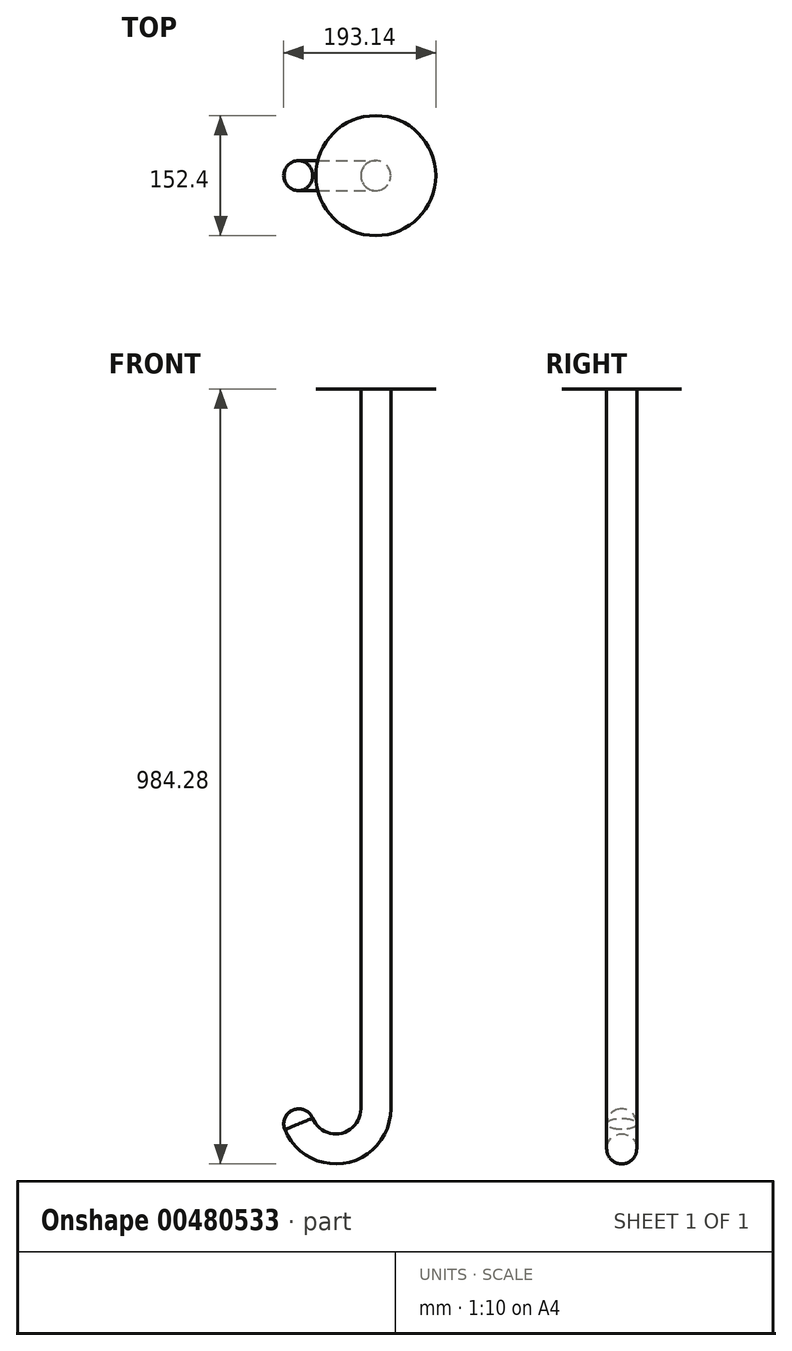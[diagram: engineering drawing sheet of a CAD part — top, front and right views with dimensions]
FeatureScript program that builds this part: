
annotation { "Feature Type Name" : "Feature", "Feature Type Description" : "" }
export const myFeature = defineFeature(function(context is Context, id is Id, definition is map)
    precondition{}
    {
        {
            var Q0;
            Q0=qCreatedBy(makeId("Top.planeOp"),FACE);
            cPlane(context, id + "F0", {"entities" : qUnion([Q0]), "cplaneType" : CPlaneType.OFFSET, "offset" : 381 * mm, "width" : 152.4 * mm, "height" : 152.4 * mm});
        }
        {
            var Q0;
            Q0=qCreatedBy(id+"F0.planeOp",FACE);
            var sketch = newSketch(context, id + "F1", { "sketchPlane" : qUnion([Q0])});
            skCircle(sketch, "E0", {"center": v(0, 0) * mm, "radius": 76.2 * mm});
            skLineSegment(sketch, "E1", {"start": v(0, 76.2) * mm, "end": v(0, -76.2) * mm, "construction": true});
            skLineSegment(sketch, "E2.1.0", {"start": v(53.88, 53.88) * mm, "end": v(-53.88, -53.88) * mm, "construction": true});
            skLineSegment(sketch, "E2.2.0", {"start": v(76.2, 0) * mm, "end": v(-76.2, 0) * mm, "construction": true});
            skLineSegment(sketch, "E2.3.0", {"start": v(53.88, -53.88) * mm, "end": v(-53.88, 53.88) * mm, "construction": true});
            skLineSegment(sketch, "E2.anchor1", {"start": v(0, 0) * mm, "end": v(0, -76.2) * mm, "construction": true});
            skLineSegment(sketch, "E2.anchor2", {"start": v(0, 0) * mm, "end": v(-53.88, 53.88) * mm, "construction": true});
            skSolve(sketch);
        }
        {
            var Q0;
            Q0=qCreatedBy(makeId("Front.planeOp"),FACE);
            var sketch = newSketch(context, id + "F2", { "sketchPlane" : qUnion([Q0])});
            skLineSegment(sketch, "E3", {"start": v(0, 0) * mm, "end": v(0, 381) * mm, "construction": true});
            skSolve(sketch);
        }
        {
            var Q0;
            Q0=qCreatedBy(makeId("Top.planeOp"),FACE);
            var sketch = newSketch(context, id + "F3", { "sketchPlane" : qUnion([Q0])});
            skCircle(sketch, "E4.cCircle", {"center": v(0, 0) * mm, "radius": 422.4 * mm, "construction": true});
            skLineSegment(sketch, "E4.0", {"start": v(323.29, 323.29) * mm, "end": v(457.2, 0) * mm});
            skLineSegment(sketch, "E4.1", {"start": v(457.2, 0) * mm, "end": v(323.29, -323.29) * mm});
            skLineSegment(sketch, "E4.2", {"start": v(323.29, -323.29) * mm, "end": v(0, -457.2) * mm});
            skLineSegment(sketch, "E4.3", {"start": v(0, -457.2) * mm, "end": v(-323.29, -323.29) * mm});
            skLineSegment(sketch, "E4.4", {"start": v(-323.29, -323.29) * mm, "end": v(-457.2, 0) * mm});
            skLineSegment(sketch, "E4.5", {"start": v(-457.2, 0) * mm, "end": v(-323.29, 323.29) * mm});
            skLineSegment(sketch, "E4.6", {"start": v(-323.29, 323.29) * mm, "end": v(0, 457.2) * mm});
            skLineSegment(sketch, "E4.7", {"start": v(0, 457.2) * mm, "end": v(323.29, 323.29) * mm});
            skPoint(sketch, "E4.0.midPoint", {"position": v(390.24, 161.64) * mm});
            skLineSegment(sketch, "E5", {"start": v(0, 457.2) * mm, "end": v(0, -457.2) * mm, "construction": true});
            skSolve(sketch);
        }
        {
            var Q0;
            Q0=qCreatedBy(makeId("Front.planeOp"),FACE);
            var sketch = newSketch(context, id + "F4", { "sketchPlane" : qUnion([Q0])});
            skArc(sketch, "E6", {"start": v(457.2, 0) * mm, "mid": v(345.6, 269.4) * mm, "end": v(76.2, 381) * mm});
            skArc(sketch, "E7.MirrorCS", {"start": v(-457.2, 0) * mm, "mid": v(-345.6, 269.4) * mm, "end": v(-76.2, 381) * mm});
            skSolve(sketch);
        }
        {
            var Q0;
            Q0=qCreatedBy(makeId("Front.planeOp"),FACE);
            var Q1;
            Q1=sQuery(id+"F2.wireOp",EDGE,"E3");
            cPlane(context, id + "F5", {"entities" : qUnion([Q0, Q1]), "cplaneType" : CPlaneType.LINE_ANGLE, "offset" : 25.4 * mm, "angle" : 45 * degree, "width" : 152.4 * mm, "height" : 152.4 * mm});
        }
        {
            var Q0;
            Q0=qCreatedBy(id+"F5.planeOp",FACE);
            var sketch = newSketch(context, id + "F6", { "sketchPlane" : qUnion([Q0])});
            skArc(sketch, "E8", {"start": v(-76.2, 381) * mm, "mid": v(-345.6, 269.4) * mm, "end": v(-457.2, 0) * mm});
            skArc(sketch, "E9.MirrorCS", {"start": v(76.2, 381) * mm, "mid": v(345.6, 269.4) * mm, "end": v(457.2, 0) * mm});
            skSolve(sketch);
        }
        {
            var Q0;
            Q0=qCreatedBy(makeId("Front.planeOp"),FACE);
            var sketch = newSketch(context, id + "F7", { "sketchPlane" : qUnion([Q0])});
            skLineSegment(sketch, "E10", {"start": v(0, 381) * mm, "end": v(0, -533.4) * mm});
            skArc(sketch, "E11", {"start": v(-101.6, -533.4) * mm, "mid": v(-50.8, -584.2) * mm, "end": v(0, -533.4) * mm});
            skSolve(sketch);
        }
        {
            var Q0;
            Q0=qCreatedBy(id+"F0.planeOp",FACE);
            var sketch = newSketch(context, id + "F8", { "sketchPlane" : qUnion([Q0])});
            skCircle(sketch, "E12", {"center": v(0, 0) * mm, "radius": 19.05 * mm});
            skSolve(sketch);
        }
        {
            var Q0;
            Q0=makeQuery(id+"F3.imprint","IMPRINT",FACE,{"disambiguationData":[TD([[makeQuery(id+"F3.imprint","IMPRINT",EDGE,{"derivedFrom":sQuery(id+"F3.wireOp",EDGE,"E4.0")}),-1.0]])]});
            var Q1;
            Q1=makeQuery(id+"F1.imprint","IMPRINT",FACE,{"disambiguationData":[TD([[makeQuery(id+"F1.imprint","IMPRINT",EDGE,{"derivedFrom":sQuery(id+"F1.wireOp",EDGE,"E0")}),1.0]])]});
            var Q2;
            Q2=sQuery(id+"F4.wireOp",EDGE,"E7.MirrorCS");
            var Q3;
            Q3=sQuery(id+"F6.wireOp",EDGE,"E9.MirrorCS");
            var Q4;
            Q4=sQuery(id+"FwEUsNg9eqqxYRy_0.1.F4.wireOp",EDGE,"E7.MirrorCS");
            var Q5;
            Q5=sQuery(id+"FwEUsNg9eqqxYRy_0.1.F6.wireOp",EDGE,"E9.MirrorCS");
            var Q6;
            Q6=sQuery(id+"F4.wireOp",EDGE,"E6");
            var Q7;
            Q7=sQuery(id+"F6.wireOp",EDGE,"E8");
            var Q8;
            Q8=sQuery(id+"FwEUsNg9eqqxYRy_0.1.F4.wireOp",EDGE,"E6");
            var Q9;
            Q9=sQuery(id+"FwEUsNg9eqqxYRy_0.1.F6.wireOp",EDGE,"E8");
            loft(context, id + "F9", {"bodyType" : ToolBodyType.SURFACE, "addGuides" : true, "wireProfilesArray" : [{ "wireProfileEntities" : qUnion([Q0]) }, { "wireProfileEntities" : qUnion([Q1]) }], "guidesArray" : [{ "guideEntities" : qUnion([Q2]), "guideDerivativeType" : LoftGuideDerivativeType.DEFAULT, "guideDerivativeMagnitude" : 1 }, { "guideEntities" : qUnion([Q3]), "guideDerivativeType" : LoftGuideDerivativeType.DEFAULT, "guideDerivativeMagnitude" : 1 }, { "guideEntities" : qUnion([Q4]), "guideDerivativeType" : LoftGuideDerivativeType.DEFAULT, "guideDerivativeMagnitude" : 1 }, { "guideEntities" : qUnion([Q5]), "guideDerivativeType" : LoftGuideDerivativeType.DEFAULT, "guideDerivativeMagnitude" : 1 }, { "guideEntities" : qUnion([Q6]), "guideDerivativeType" : LoftGuideDerivativeType.DEFAULT, "guideDerivativeMagnitude" : 1 }, { "guideEntities" : qUnion([Q7]), "guideDerivativeType" : LoftGuideDerivativeType.DEFAULT, "guideDerivativeMagnitude" : 1 }, { "guideEntities" : qUnion([Q8]), "guideDerivativeType" : LoftGuideDerivativeType.DEFAULT, "guideDerivativeMagnitude" : 1 }, { "guideEntities" : qUnion([Q9]), "guideDerivativeType" : LoftGuideDerivativeType.DEFAULT, "guideDerivativeMagnitude" : 1 }]});
        }
        {
            var Q0;
            Q0=makeQuery(id+"F8.imprint","IMPRINT",FACE,{"disambiguationData":[TD([[makeQuery(id+"F8.imprint","IMPRINT",EDGE,{"derivedFrom":sQuery(id+"F8.wireOp",EDGE,"E12")}),1.0]])]});
            var Q1;
            Q1=sQuery(id+"F7.wireOp",EDGE,"E10");
            var Q2;
            Q2=sQuery(id+"F7.wireOp",EDGE,"E11");
            sweep(context, id + "F10", {"profiles" : qUnion([Q0]), "path" : qUnion([Q1, Q2])});
        }
        {
            var Q0;
            Q0=makeQuery(id+"F10.opSweep","CAP_EDGE",EDGE,{"disambiguationData":[OSD([sQuery(id+"F7.wireOp",VERTEX,"E11.start"),sQuery(id+"F8.wireOp",EDGE,"E12")])],"isStart":false});
            fillet(context, id + "F11", {"entities" : qUnion([Q0]), "radius" : 19.05 * mm, "tangentPropagation" : true, "allowEdgeOverflow" : false});
        }
        {
            var Q0;
            Q0=makeQuery(id+"F1.imprint","IMPRINT",FACE,{"disambiguationData":[TD([[makeQuery(id+"F1.imprint","IMPRINT",EDGE,{"derivedFrom":sQuery(id+"F1.wireOp",EDGE,"E0")}),1.0]])]});
            extrude(context, id + "F12", {"entities" : qUnion([Q0]), "operationType" : NewBodyOperationType.ADD, "depth" : 0.03 * mm});
        }
    });
